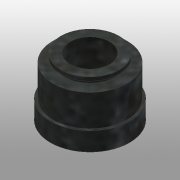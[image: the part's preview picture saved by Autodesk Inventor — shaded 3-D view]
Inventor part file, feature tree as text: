
AUTODESK INVENTOR PART (.ipt)
format: ipt  version: 2015 (Build 190159000, 159)  size: 137,728 bytes
history: native  units: mm
features: other x3, sketch x2
ambient origin geometry x8: Origin, YZ Plane, XZ Plane, XY Plane, X Axis, Y Axis, Z Axis, Center Point
bodies: Solid1 (feature_tree)
feature tree (5):
  other  "500-107.ipt"
  other  "Solid1::500-107.ipt"
  other  "TaggingFeature1"
  sketch  "Sketch1"  dims[d0=10.0mm]
  sketch  "Sketch3"
